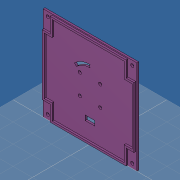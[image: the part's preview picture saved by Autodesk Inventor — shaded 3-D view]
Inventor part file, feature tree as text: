
AUTODESK INVENTOR PART (.ipt)
format: ipt  version: 2019 (Build 230136000, 136)  size: 178,176 bytes
history: native  units: mm
features: extrude x3, sketch x2, hole x1
ambient origin geometry x8: Origin, YZ Plane, XZ Plane, XY Plane, X Axis, Y Axis, Z Axis, Center Point
bodies: Volumenkörper1 (feature_tree)
feature tree (6):
  sketch  "Skizze1"  dims[d0=97.6mm d3=2.0mm d4=0.0mm]
  extrude  "Extrusion1"  Depth=2.0mm TaperAngle=0.0deg
  hole  "Bohrung1"  [1 undecoded]
  extrude  "Extrusion4"  Depth=2.0mm
  extrude  "Extrusion5"  Depth=2.0mm
  sketch  "Skizze2"  dims[d20=3.4mm d21=6.0mm d22=4.0mm d23=2.0mm d24=90.0deg d25=8.0mm d26=20.594885mm d43=2.0mm d44=0.0mm d45=100.0mm d46=100.0mm d47=40.0mm d51=4.0mm d52=0.0mm d53=3.0mm d54=45.0deg d55=30.0mm d57=10.0mm d58=5.0mm d59=25.0mm d61=100.0mm d62=95.5mm d63=18.5mm d64=10.5mm d65=2.0mm d67=6.0mm]
note: 1 required parameter value undecoded (feature->parameter linkage not recoverable at this tier; creation-order binding heuristic only, values carry confidence <= 0.55)
